# Revit family: Gira_211400
name_source: partatom
category: Electrical Fixtures
revit_build: Autodesk Revit 2017 (Build: 20160225_1515(x64)
units: mm (PartAtom-declared; Revit-internal decimal feet)

## family parameters
Cut with Voids When Loaded = No
Host = Face
Maintain Annotation Orientation = No
Part Type = Normal
Room Calculation Point = No
Round Connector Dimension = Use Diameter
Shared = No

## types (1)
- Heat.act. Basic 6-g KNX DRA
    BIM = https://media.live.bim.site 8f.rfa
    BIMSITE_PRODUCT_ID = a8b0bfac80ab459d18165d86efc775a7bda54a18
    Bus connection included = No
    Cost = 0 $
    Default Elevation = 1219 mm
    Description = Heat.act.Basic 6g DRA KNX KNX heating actuator Basic, 6-gang,DRA plus Features: - Heating actuator for switching electrothermic servos for heating or cooling ceilings. - Control using 1-bit or 1-byte corrected variable telegrams. - For 1-byte correcting variables, the outputs are controlled by pulse width modulation (PWM). - Servos with the characteristic de-energised open" or "de-energised closed" can be controlled. - Servos can be activated with rated voltage 24 V or 230 V. - Overload protected, short-circuit protected. - Standard protection. - Feedback via bus e.g. for overload and short circuit. - Switching the heating circuit pump (standard functions). - Passive group feedback of the closed servos.,Notes : - Valves with the same operating voltage must be connected at all outputs. - VDE approval in accordance with EN 60669-1, EN 60669-2-1. - Installation on DIN top-hat rail."
    GTIN = 4010337018414
    HAN = 211400
    Handschaltung = No
    HeinzeBIM = https://www.heinze.de
    Local operation/hand operation = No
    Manufacturer = Gira
    Max. number of venetian-blind outputs = 0
    Number of binary inputs = 0
    Number of inputs = 0
    Number of outputs = 0
    Rated current [Ampere] = 0
    Stellgröße schaltend = Yes
    Stellgröße stetig = No
    Suitable for C-load = No
    URL = https://www.gira.de
    Ventilschutzfunktion = No
    With switch function = No

## geometry (parser evidence)
native form markers: Blend x2, Sweep x3
no freeform markers — native parametric forms only
